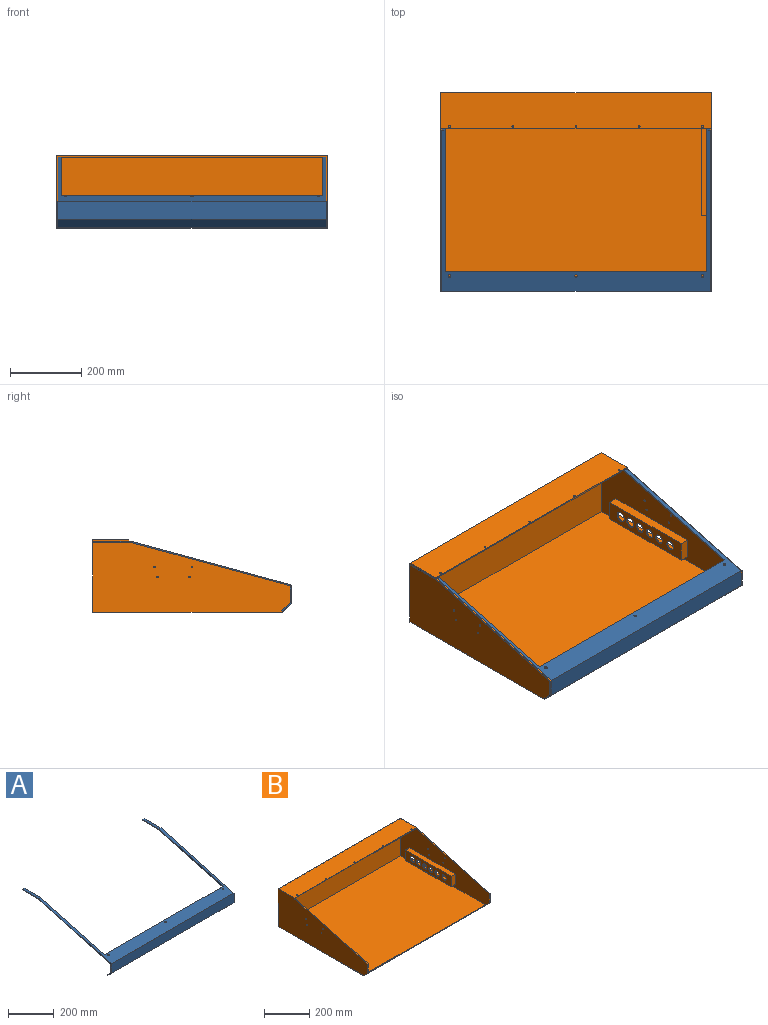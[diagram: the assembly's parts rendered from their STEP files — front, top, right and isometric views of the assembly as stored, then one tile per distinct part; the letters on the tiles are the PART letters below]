
ASSEMBLY  parts=2 mates=1
PART A: 21 faces, bbox 762x555.6x199.1 mm
  f0: plane 736.6x3.06mm, normal (0,0.96,0.26), area 2338.7mm2, adj f3,f4,f16,f20
  f1: plane 762x23.54mm, normal (0,0.71,0.71), area 25367.6mm2, adj f2,f7,f8,f9
  f2: plane 762x47.06mm, normal (0,1,0), area 35860mm2, adj f1,f3,f8,f9
  f3: plane 762x450.87mm, normal (0,0.26,-0.96), area 52047.9mm2, adj f0,f2,f8,f9,f10,f11,f12,f14
  f4: plane 762x453.62mm, normal (0,-0.26,0.96), area 53906.2mm2, adj f0,f5,f8,f9,f10,f11,f12,f13
  f5: plane 762x50.8mm, normal (0,-1,0), area 38709.6mm2, adj f4,f6,f8,f9
  f6: plane 762x24.47mm, normal (0,-0.71,-0.71), area 26369.7mm2, adj f5,f7,f8,f9
  f7: plane 762x2.25mm, normal (0,0.71,-0.71), area 2419.3mm2, adj f1,f6,f8,f9
  f8: plane 555.63x199.1mm, normal (1,0,0), area 2074.7mm2, adj f1,f2,f3,f4,f5,f6,f7,f17
  f9: plane 555.63x199.1mm, normal (-1,0,0), area 2074.7mm2, adj f1,f2,f3,f4,f5,f6,f7,f13
  f10: cylinder r=3.77mm len=8.11mm, axis (0,-0.26,0.96), area 75.2mm2, adj f3,f4
  f11: cylinder r=3.77mm len=8.11mm, axis (0,-0.26,0.96), area 75.2mm2, adj f3,f4
  f12: cylinder r=3.77mm len=8.11mm, axis (0,-0.26,0.96), area 75.2mm2, adj f3,f4
  f13: plane 102.01x12.7mm, normal (0,0,1), area 1295.5mm2, adj f4,f9,f15,f16
  f14: plane 101.58x12.7mm, normal (0,0,-1), area 1290.1mm2, adj f3,f9,f15,f16
  f15: plane 12.7x3.18mm, normal (0,1,0), area 40.3mm2, adj f9,f13,f14,f16
  f16: plane 500.49x111.84mm, normal (1,0,0), area 1634mm2, adj f0,f3,f4,f13,f14,f15
  f17: plane 102.01x12.7mm, normal (0,0,1), area 1295.5mm2, adj f4,f8,f19,f20
  f18: plane 101.58x12.7mm, normal (0,0,-1), area 1290.1mm2, adj f3,f8,f19,f20
  f19: plane 12.7x3.18mm, normal (0,1,0), area 40.3mm2, adj f8,f17,f18,f20
  f20: plane 500.49x111.84mm, normal (-1,0,0), area 1634mm2, adj f0,f3,f4,f17,f18,f19
PART B: 48 faces, bbox 762x558.8x203.2 mm
  f0: plane 50.8x25.4mm, normal (0,-1,0), area 1290.3mm2, adj f1,f3,f13,f36
  f1: plane 279.4x25.4mm, normal (0,0,1), area 7096.8mm2, adj f0,f2,f13,f36
  f2: plane 50.8x25.4mm, normal (0,1,0), area 1290.3mm2, adj f1,f3,f13,f36
  f3: plane 279.4x25.4mm, normal (0,0,-1), area 7096.8mm2, adj f0,f2,f13,f36
  f4: plane 755.65x2.25mm, normal (0,-0.71,0.71), area 2399.2mm2, adj f6,f8,f18,f22
  f5: plane 755.65x196.85mm, normal (0,-1,0), area 148749.7mm2, adj f6,f7,f18,f22
  f6: plane 755.65x528.91mm, normal (0,0,1), area 399670.7mm2, adj f4,f5,f18,f22
  f7: plane 755.65x98.43mm, normal (0,0,-1), area 74272.5mm2, adj f5,f12,f18,f22,f43,f44,f45,f46
  f8: plane 762x25.4mm, normal (0,-0.71,-0.71), area 1221.9mm2, adj f4,f9,f13,f14,f16,f18,f21,f22
  f9: plane 762x533.4mm, normal (0,0,-1), area 406450.8mm2, adj f8,f10,f13,f14
  f10: plane 762x203.2mm, normal (0,1,0), area 154838.4mm2, adj f9,f11,f13,f14
  f11: plane 762x101.6mm, normal (0,0,1), area 77316.8mm2, adj f10,f12,f13,f14,f43,f44,f45,f46
  f12: plane 762x3.18mm, normal (0,-1,0), area 2419.3mm2, adj f7,f11,f13,f14,f17,f19
  f13: plane 558.8x203.2mm, normal (1,0,0), area 69412.3mm2, adj f0,f1,f2,f3,f8,f9,f10,f11
  f14: plane 558.8x203.2mm, normal (-1,0,0), area 83605.8mm2, adj f8,f9,f10,f11,f12,f15,f16,f17
  f15: plane 453.62x123.83mm, normal (0,-0.26,0.96), area 1492.9mm2, adj f14,f16,f17,f18
  f16: plane 50.8x3.18mm, normal (0,-1,0), area 161.3mm2, adj f8,f14,f15,f18
  f17: plane 3.58x3.18mm, normal (0,0,1), area 11.4mm2, adj f12,f14,f15,f18
  f18: plane 555.63x199.1mm, normal (1,0,0), area 80964.7mm2, adj f4,f5,f6,f7,f8,f15,f16,f17
  f19: plane 3.58x3.18mm, normal (0,0,1), area 11.4mm2, adj f12,f13,f20,f22
  f20: plane 453.62x123.83mm, normal (0,-0.26,0.96), area 1492.9mm2, adj f13,f19,f21,f22
  f21: plane 50.8x3.18mm, normal (0,-1,0), area 161.3mm2, adj f8,f13,f20,f22
  f22: plane 555.63x199.1mm, normal (-1,0,0), area 64634.1mm2, adj f4,f5,f6,f7,f8,f19,f20,f21
  f23: cylinder r=2.58mm len=5.16mm, axis (-1,0,0), area 51.4mm2, adj f13,f22
  f24: cylinder r=2.58mm len=5.16mm, axis (-1,0,0), area 51.4mm2, adj f13,f22
  f25: cylinder r=2.58mm len=5.16mm, axis (-1,0,0), area 51.4mm2, adj f13,f22
  f26: cylinder r=2.58mm len=5.16mm, axis (-1,0,0), area 51.4mm2, adj f13,f22
  f27: cylinder r=2.58mm len=5.16mm, axis (-1,0,0), area 51.4mm2, adj f14,f18
  f28: cylinder r=2.58mm len=5.16mm, axis (-1,0,0), area 51.4mm2, adj f14,f18
  f29: cylinder r=2.58mm len=5.16mm, axis (-1,0,0), area 51.4mm2, adj f14,f18
  f30: cylinder r=2.58mm len=5.16mm, axis (-1,0,0), area 51.4mm2, adj f14,f18
  f31: plane 57.15x25.4mm, normal (0,-1,0), area 1451.6mm2, adj f22,f32,f34,f35
  f32: plane 285.75x25.4mm, normal (0,0,-1), area 7258mm2, adj f22,f31,f33,f35
  f33: plane 57.15x25.4mm, normal (0,1,0), area 1451.6mm2, adj f22,f32,f34,f35
  f34: plane 285.75x25.4mm, normal (0,0,1), area 7258mm2, adj f22,f31,f33,f35
  f35: plane 285.75x57.15mm, normal (-1,0,0), area 12959.9mm2, adj f31,f32,f33,f34,f37,f38,f39,f40
  f36: plane 279.4x50.8mm, normal (1,0,0), area 10822.8mm2, adj f0,f1,f2,f3,f37,f38,f39,f40
  f37: cylinder r=12.89mm len=25.78mm, axis (-1,0,0), area 257.2mm2, adj f35,f36
  f38: cylinder r=12.89mm len=25.78mm, axis (-1,0,0), area 257.2mm2, adj f35,f36
  f39: cylinder r=12.89mm len=25.78mm, axis (-1,0,0), area 257.2mm2, adj f35,f36
  f40: cylinder r=12.89mm len=25.78mm, axis (-1,0,0), area 257.2mm2, adj f35,f36
  f41: cylinder r=14.29mm len=28.58mm, axis (-1,0,0), area 285mm2, adj f35,f36
  f42: cylinder r=14.29mm len=28.58mm, axis (-1,0,0), area 285mm2, adj f35,f36
  f43: cylinder r=2.55mm len=5.11mm, axis (0,0,1), area 50.9mm2, adj f7,f11
  f44: cylinder r=2.55mm len=5.11mm, axis (0,0,1), area 50.9mm2, adj f7,f11
  f45: cylinder r=2.55mm len=5.11mm, axis (0,0,1), area 50.9mm2, adj f7,f11
  f46: cylinder r=2.55mm len=5.11mm, axis (0,0,1), area 50.9mm2, adj f7,f11
  f47: cylinder r=2.55mm len=5.11mm, axis (0,0,1), area 50.9mm2, adj f7,f11
PLACE A t=(-381,-266.7,0)mm
PLACE B t=(-381,-266.7,0)mm
MATE fastened B.f4 <-> A.f7  axis (0,-0.71,0.71) through (0,-267.63,0.93)mm
